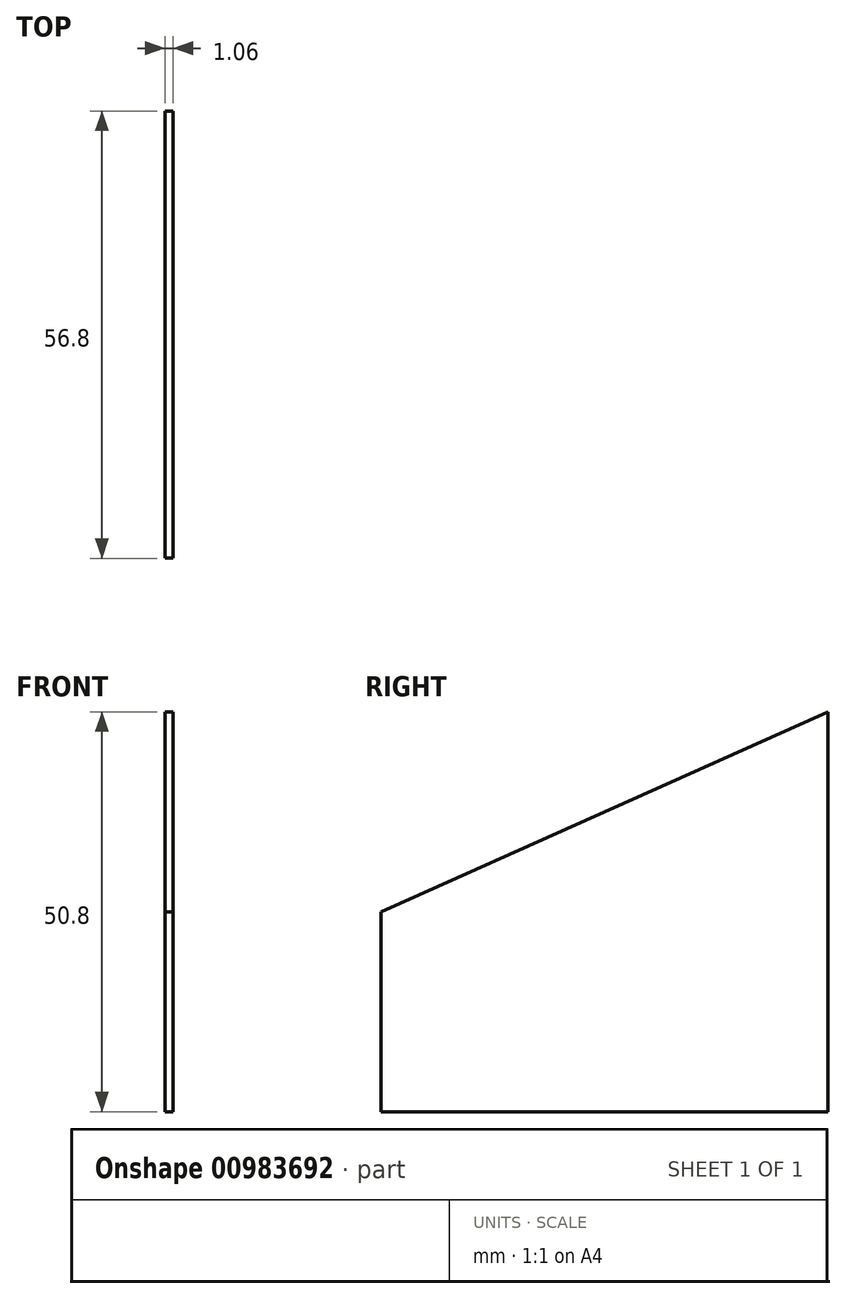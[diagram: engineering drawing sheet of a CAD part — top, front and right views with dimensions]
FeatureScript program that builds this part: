
annotation { "Feature Type Name" : "Feature", "Feature Type Description" : "" }
export const myFeature = defineFeature(function(context is Context, id is Id, definition is map)
    precondition{}
    {
        {
            var Q0;
            Q0=qCreatedBy(makeId("Right.planeOp"),FACE);
            var sketch = newSketch(context, id + "F0", { "sketchPlane" : qUnion([Q0])});
            skLineSegment(sketch, "E0.top", {"start": v(28.4, -12.7) * mm, "end": v(-28.4, -12.7) * mm});
            skLineSegment(sketch, "E0.left", {"start": v(28.4, 12.7) * mm, "end": v(28.4, -12.7) * mm});
            skLineSegment(sketch, "E0.right", {"start": v(-28.4, 12.7) * mm, "end": v(-28.4, -12.7) * mm});
            skPoint(sketch, "E0.middle", {"position": v(0, 0) * mm});
            skLineSegment(sketch, "E1", {"start": v(28.4, 12.7) * mm, "end": v(28.4, 38.1) * mm});
            skLineSegment(sketch, "E2", {"start": v(28.4, 38.1) * mm, "end": v(-28.4, 12.7) * mm});
            skSolve(sketch);
        }
        {
            var Q0;
            Q0 = qSketchRegion(id + "F0", true);
            extrude(context, id + "F1", {"entities" : qUnion([Q0]), "depth" : 1.06 * mm, "offsetDistance" : 25.4 * mm});
        }
    });
